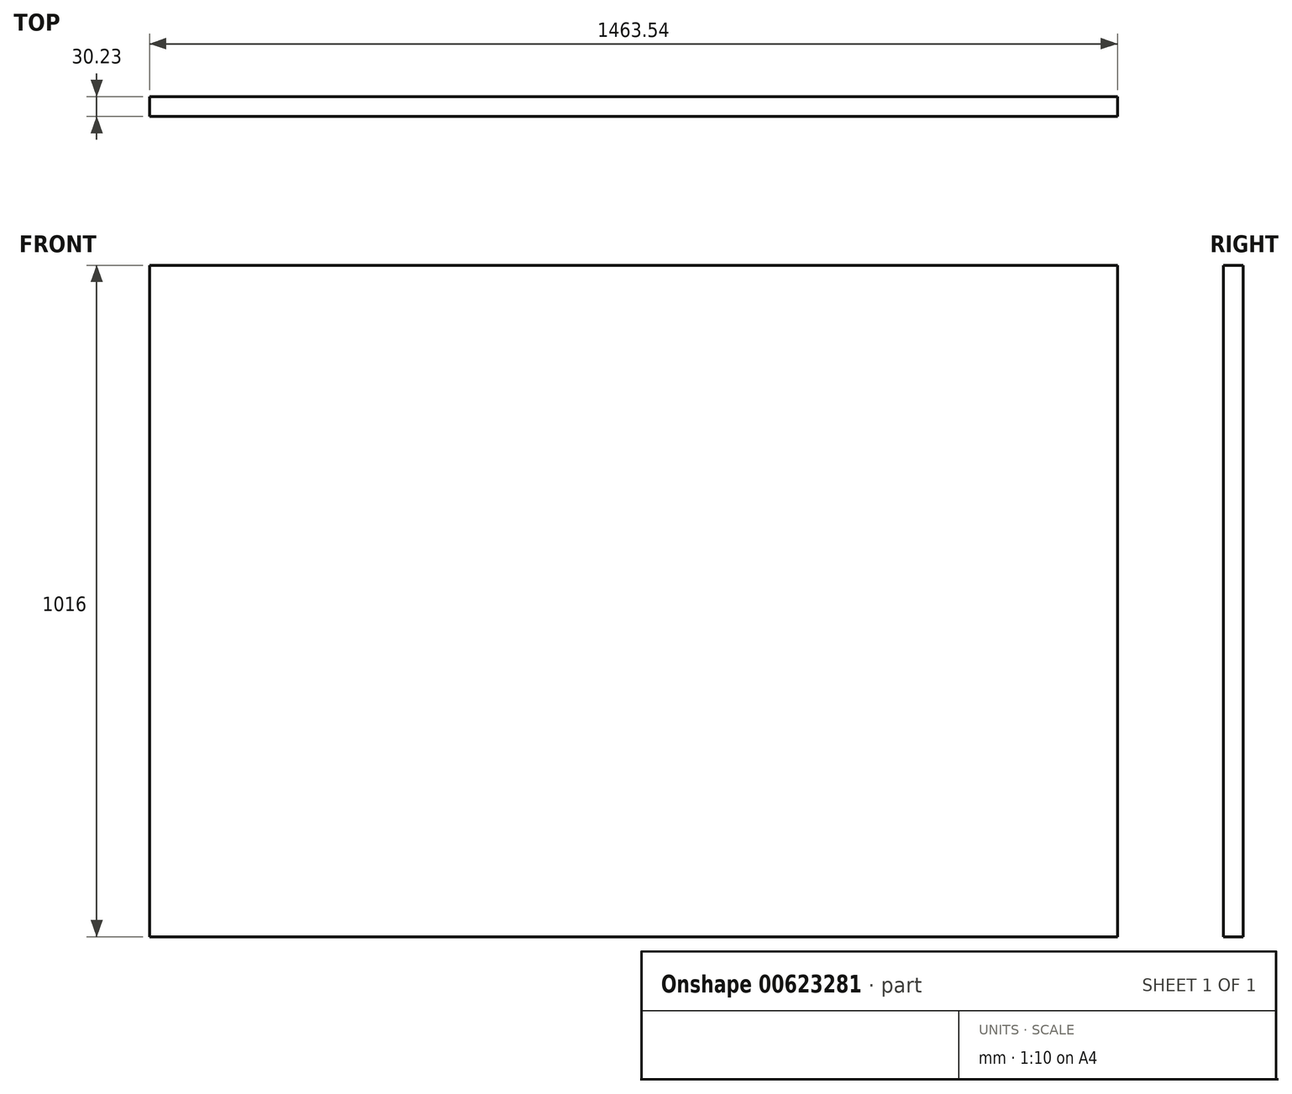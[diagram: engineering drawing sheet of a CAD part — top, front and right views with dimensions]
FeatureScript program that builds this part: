
annotation { "Feature Type Name" : "Feature", "Feature Type Description" : "" }
export const myFeature = defineFeature(function(context is Context, id is Id, definition is map)
    precondition{}
    {
        {
            var Q0;
            Q0=qCreatedBy(makeId("Front.planeOp"),FACE);
            var sketch = newSketch(context, id + "F0", { "sketchPlane" : qUnion([Q0])});
            skLineSegment(sketch, "E0.bottom", {"start": v(-731.77, 508) * mm, "end": v(731.77, 508) * mm});
            skLineSegment(sketch, "E0.top", {"start": v(-731.77, -508) * mm, "end": v(731.77, -508) * mm});
            skLineSegment(sketch, "E0.left", {"start": v(-731.77, 508) * mm, "end": v(-731.77, -508) * mm});
            skLineSegment(sketch, "E0.right", {"start": v(731.77, 508) * mm, "end": v(731.77, -508) * mm});
            skPoint(sketch, "E0.middle", {"position": v(0, 0) * mm});
            skSolve(sketch);
        }
        {
            var Q0;
            Q0=makeQuery(id+"F0.imprint","IMPRINT",FACE,{"disambiguationData":[TD([[makeQuery(id+"F0.imprint","IMPRINT",EDGE,{"derivedFrom":sQuery(id+"F0.wireOp",EDGE,"E0.bottom")}),-1.0]])]});
            extrude(context, id + "F1", {"entities" : qUnion([Q0]), "depth" : 30.23 * mm, "offsetDistance" : 25.4 * mm});
        }
    });
